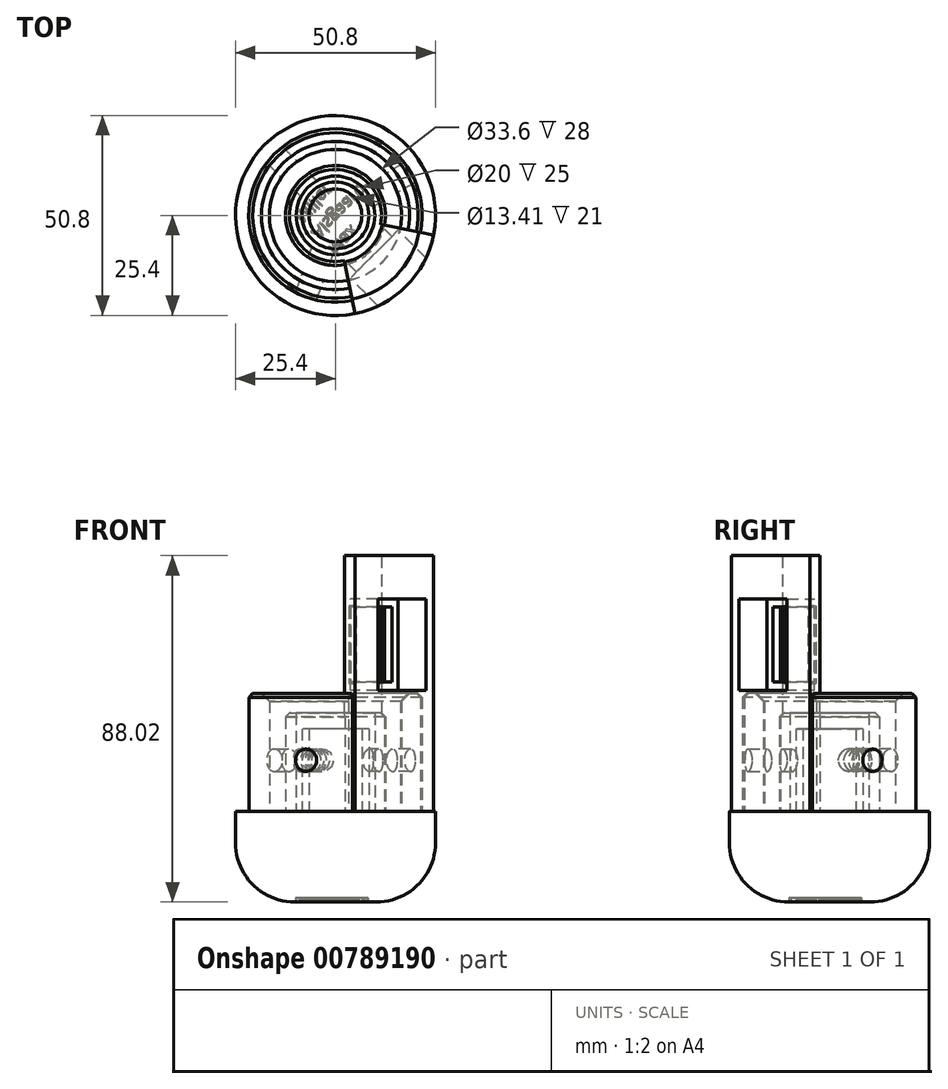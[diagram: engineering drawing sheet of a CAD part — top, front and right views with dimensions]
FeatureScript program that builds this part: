
annotation { "Feature Type Name" : "Feature", "Feature Type Description" : "" }
export const myFeature = defineFeature(function(context is Context, id is Id, definition is map)
    precondition{}
    {
        {
            var Q0;
            Q0=qCreatedBy(makeId("Right.planeOp"),FACE);
            var sketch = newSketch(context, id + "F0", { "sketchPlane" : qUnion([Q0])});
            skLineSegment(sketch, "E0", {"start": v(0, 22.52) * mm, "end": v(0, -20.14) * mm, "construction": true});
            skSolve(sketch);
        }
        {
            var Q0;
            Q0=qCreatedBy(makeId("Top.planeOp"),FACE);
            var sketch = newSketch(context, id + "F1", { "sketchPlane" : qUnion([Q0])});
            skCircle(sketch, "E1", {"center": v(0, 0) * mm, "radius": 25.4 * mm});
            skCircle(sketch, "E2", {"center": v(0, 0) * mm, "radius": 22.03 * mm});
            skCircle(sketch, "E3", {"center": v(0, 0) * mm, "radius": 16.8 * mm});
            skCircle(sketch, "E4", {"center": v(0, 0) * mm, "radius": 12.69 * mm});
            skCircle(sketch, "E5", {"center": v(0, 0) * mm, "radius": 10 * mm});
            skSolve(sketch);
        }
        {
            var Q0;
            Q0=qCreatedBy(makeId("Right.planeOp"),FACE);
            var Q1;
            Q1=sQuery(id+"F0.wireOp",EDGE,"E0");
            cPlane(context, id + "F2", {"entities" : qUnion([Q0, Q1]), "cplaneType" : CPlaneType.LINE_ANGLE, "offset" : 25 * mm, "angle" : 30 * degree, "oppositeDirection" : true, "width" : 150 * mm, "height" : 150 * mm});
        }
        {
            var Q0;
            Q0=qCreatedBy(makeId("Front.planeOp"),FACE);
            var Q1;
            Q1=sQuery(id+"F0.wireOp",EDGE,"E0");
            cPlane(context, id + "F3", {"entities" : qUnion([Q0, Q1]), "cplaneType" : CPlaneType.LINE_ANGLE, "offset" : 25 * mm, "angle" : 20 * degree, "width" : 150 * mm, "height" : 150 * mm});
        }
        {
            var Q0;
            Q0=makeQuery(id+"F1.imprint","IMPRINT",FACE,{"disambiguationData":[TD([[makeQuery(id+"F1.imprint","IMPRINT",EDGE,{"derivedFrom":sQuery(id+"F1.wireOp",EDGE,"E1")}),1.0]])]});
            var Q1;
            Q1=makeQuery(id+"F1.imprint","IMPRINT",FACE,{"disambiguationData":[TD([[makeQuery(id+"F1.imprint","IMPRINT",EDGE,{"derivedFrom":sQuery(id+"F1.wireOp",EDGE,"E2")}),1.0]])]});
            var Q2;
            Q2=makeQuery(id+"F1.imprint","IMPRINT",FACE,{"disambiguationData":[TD([[makeQuery(id+"F1.imprint","IMPRINT",EDGE,{"derivedFrom":sQuery(id+"F1.wireOp",EDGE,"E3")}),1.0]])]});
            var Q3;
            Q3=makeQuery(id+"F1.imprint","IMPRINT",FACE,{"disambiguationData":[TD([[makeQuery(id+"F1.imprint","IMPRINT",EDGE,{"derivedFrom":sQuery(id+"F1.wireOp",EDGE,"E4")}),1.0]])]});
            var Q4;
            Q4=makeQuery(id+"F1.imprint","IMPRINT",FACE,{"disambiguationData":[TD([[makeQuery(id+"F1.imprint","IMPRINT",EDGE,{"derivedFrom":sQuery(id+"F1.wireOp",EDGE,"E5")}),1.0]])]});
            extrude(context, id + "F4", {"entities" : qUnion([Q0, Q1, Q2, Q3, Q4]), "oppositeDirection" : true, "depth" : 8 * mm, "offsetDistance" : 25 * mm});
        }
        {
            var Q0;
            Q0=makeQuery(id+"F1.imprint","IMPRINT",FACE,{"disambiguationData":[TD([[makeQuery(id+"F1.imprint","IMPRINT",EDGE,{"derivedFrom":sQuery(id+"F1.wireOp",EDGE,"E2")}),1.0]])]});
            extrude(context, id + "F5", {"entities" : qUnion([Q0]), "operationType" : NewBodyOperationType.ADD, "depth" : 30 * mm, "offsetDistance" : 25 * mm});
        }
        {
            var Q0;
            Q0=makeQuery(id+"F1.imprint","IMPRINT",FACE,{"disambiguationData":[TD([[makeQuery(id+"F1.imprint","IMPRINT",EDGE,{"derivedFrom":sQuery(id+"F1.wireOp",EDGE,"E4")}),1.0]])]});
            extrude(context, id + "F6", {"entities" : qUnion([Q0]), "operationType" : NewBodyOperationType.ADD, "depth" : 25 * mm, "offsetDistance" : 25 * mm});
        }
        {
            var Q0;
            Q0=qCreatedBy(id+"F2.planeOp",FACE);
            var sketch = newSketch(context, id + "F7", { "sketchPlane" : qUnion([Q0])});
            skCircle(sketch, "E6", {"center": v(0, 13) * mm, "radius": 2.85 * mm});
            skSolve(sketch);
        }
        {
            var Q0;
            Q0=qCreatedBy(id+"F3.planeOp",FACE);
            var sketch = newSketch(context, id + "F8", { "sketchPlane" : qUnion([Q0])});
            skCircle(sketch, "E7", {"center": v(0, 13) * mm, "radius": 2.85 * mm});
            skLineSegment(sketch, "E8", {"start": v(0, -1.69) * mm, "end": v(0, 3.4) * mm, "construction": true});
            skSolve(sketch);
        }
        {
            var Q0;
            Q0=qSketchRegion(id+"F8",true);
            extrude(context, id + "F9", {"entities" : qUnion([Q0]), "operationType" : NewBodyOperationType.REMOVE, "oppositeDirection" : true, "depth" : 25 * mm, "offsetDistance" : 25 * mm, "hasSecondDirection" : true, "secondDirectionOppositeDirection" : false, "secondDirectionDepth" : 0 * mm});
        }
        {
            var Q0;
            Q0=qSketchRegion(id+"F7",true);
            var Q1;
            Q1=sQuery(id+"F7.wireOp",EDGE,"E6");
            extrude(context, id + "F10", {"entities" : qUnion([Q0]), "operationType" : NewBodyOperationType.REMOVE, "surfaceEntities" : qUnion([Q1]), "depth" : 0 * mm, "offsetDistance" : 25 * mm, "hasSecondDirection" : true, "secondDirectionOppositeDirection" : true, "secondDirectionDepth" : 25 * mm});
        }
        {
            var Q0;
            Q0=qCreatedBy(makeId("Front.planeOp"),FACE);
            var Q1;
            Q1=qCreatedBy(makeId("Right.planeOp"),FACE);
            cPlane(context, id + "F11", {"entities" : qUnion([Q0, Q1]), "cplaneType" : CPlaneType.MID_PLANE, "offset" : 25 * mm, "width" : 150 * mm, "height" : 150 * mm});
        }
        {
            var Q0;
            Q0=qCreatedBy(id+"F11.planeOp",FACE);
            var sketch = newSketch(context, id + "F12", { "sketchPlane" : qUnion([Q0])});
            skLineSegment(sketch, "E9", {"start": v(21.68, 65) * mm, "end": v(21.68, 0) * mm});
            skLineSegment(sketch, "E10", {"start": v(21.68, 0) * mm, "end": v(25.41, 0) * mm});
            skLineSegment(sketch, "E11", {"start": v(25.41, 0) * mm, "end": v(25.41, 65) * mm});
            skLineSegment(sketch, "E12", {"start": v(25.41, 65) * mm, "end": v(21.68, 65) * mm});
            skLineSegment(sketch, "E13.bottom", {"start": v(21.68, 0.02) * mm, "end": v(12.08, 0.02) * mm});
            skLineSegment(sketch, "E13.top", {"start": v(21.68, 65.02) * mm, "end": v(12.08, 65.02) * mm});
            skLineSegment(sketch, "E13.left", {"start": v(21.68, 0.02) * mm, "end": v(21.68, 65.02) * mm});
            skLineSegment(sketch, "E13.right", {"start": v(12.08, 0.02) * mm, "end": v(12.08, 65.02) * mm});
            skSolve(sketch);
        }
        {
            var Q0;
            {var subQ1=sQuery(id+"F12.wireOp",EDGE,"E9");Q0=makeQuery(id+"F12.imprint","IMPRINT",FACE,{"disambiguationData":[TD([[makeQuery(id+"F12.imprint","IMPRINT",EDGE,{"derivedFrom":subQ1}),1.0]])]});}
            var Q1;
            {var subQ3=sQuery(id+"F12.wireOp",EDGE,"E13.bottom");Q1=makeQuery(id+"F12.imprint","IMPRINT",FACE,{"disambiguationData":[TD([[makeQuery(id+"F12.imprint","IMPRINT",EDGE,{"derivedFrom":subQ3}),-1.0]])]});}
            var Q2;
            Q2=sQuery(id+"F8.wireOp",EDGE,"E8");
            revolve(context, id + "F13", {"operationType" : NewBodyOperationType.ADD, "surfaceOperationType" : NewSurfaceOperationType.NEW, "entities" : qUnion([Q0, Q1]), "axis" : qUnion([Q2]), "revolveType" : RevolveType.SYMMETRIC, "angle" : 67.67 * degree});
        }
        {
            var Q0;
            Q0=qCreatedBy(id+"F11.planeOp",FACE);
            var sketch = newSketch(context, id + "F14", { "sketchPlane" : qUnion([Q0])});
            skLineSegment(sketch, "E14.bottom", {"start": v(25.41, 30.8) * mm, "end": v(13.91, 30.8) * mm});
            skLineSegment(sketch, "E14.top", {"start": v(25.41, 54) * mm, "end": v(13.91, 54) * mm});
            skLineSegment(sketch, "E14.left", {"start": v(25.41, 30.8) * mm, "end": v(25.41, 54) * mm});
            skLineSegment(sketch, "E14.right", {"start": v(13.91, 30.8) * mm, "end": v(13.91, 54) * mm});
            skLineSegment(sketch, "E15", {"start": v(25.41, 65) * mm, "end": v(25.41, 0) * mm});
            skLineSegment(sketch, "E16", {"start": v(25.41, 65) * mm, "end": v(25.41, 0) * mm, "construction": true});
            skSolve(sketch);
        }
        {
            var Q0;
            Q0=qSketchRegion(id+"F14",true);
            extrude(context, id + "F15", {"entities" : qUnion([Q0]), "operationType" : NewBodyOperationType.REMOVE, "oppositeDirection" : true, "depth" : 8.6 * mm, "offsetDistance" : 25 * mm, "hasSecondDirection" : true, "secondDirectionOppositeDirection" : false, "secondDirectionDepth" : 8.6 * mm});
        }
        {
            var Q0;
            Q0=qCreatedBy(makeId("Right.planeOp"),FACE);
            var Q1;
            Q1=qCreatedBy(makeId("Front.planeOp"),FACE);
            cPlane(context, id + "F16", {"entities" : qUnion([Q0, Q1]), "cplaneType" : CPlaneType.MID_PLANE, "offset" : 25 * mm, "flipAlignment" : true, "width" : 150 * mm, "height" : 150 * mm});
        }
        {
            var Q0;
            Q0=qCreatedBy(id+"F16.planeOp",FACE);
            cPlane(context, id + "F17", {"entities" : qUnion([Q0]), "cplaneType" : CPlaneType.OFFSET, "offset" : 25.4 * mm, "width" : 150 * mm, "height" : 150 * mm});
        }
        {
            var Q0;
            Q0=qCreatedBy(id+"F11.planeOp",FACE);
            var sketch = newSketch(context, id + "F18", { "sketchPlane" : qUnion([Q0])});
            skLineSegment(sketch, "E17.0", {"start": v(13.91, 30.8) * mm, "end": v(13.91, 54) * mm});
            skLineSegment(sketch, "E18.0", {"start": v(25.41, 54) * mm, "end": v(13.91, 54) * mm});
            skLineSegment(sketch, "E19.0", {"start": v(25.41, 30.8) * mm, "end": v(13.91, 30.8) * mm});
            skLineSegment(sketch, "E20.bottom", {"start": v(13.91, 51.9) * mm, "end": v(11.22, 51.9) * mm});
            skLineSegment(sketch, "E20.top", {"start": v(13.91, 32.9) * mm, "end": v(11.22, 32.9) * mm});
            skLineSegment(sketch, "E20.left", {"start": v(13.91, 51.9) * mm, "end": v(13.91, 32.9) * mm});
            skLineSegment(sketch, "E20.right", {"start": v(11.22, 51.9) * mm, "end": v(11.22, 32.9) * mm});
            skSolve(sketch);
        }
        {
            var Q0;
            Q0=makeQuery(id+"F18.imprint","IMPRINT",FACE,{"disambiguationData":[TD([[makeQuery(id+"F18.imprint","IMPRINT",EDGE,{"derivedFrom":sQuery(id+"F18.wireOp",EDGE,"E20.bottom")}),1.0]])]});
            extrude(context, id + "F19", {"entities" : qUnion([Q0]), "operationType" : NewBodyOperationType.REMOVE, "endBound" : BoundingType.SYMMETRIC, "oppositeDirection" : true, "depth" : 12.68 * mm, "offsetDistance" : 25 * mm});
        }
        {
            var Q0;
            Q0=qCreatedBy(id+"F11.planeOp",FACE);
            var sketch = newSketch(context, id + "F20", { "sketchPlane" : qUnion([Q0])});
            skLineSegment(sketch, "E21.0.0", {"start": v(25.41, 30.8) * mm, "end": v(25.41, 54) * mm});
            skLineSegment(sketch, "E21.0.1", {"start": v(25.41, 54) * mm, "end": v(13.91, 54) * mm});
            skLineSegment(sketch, "E21.0.2", {"start": v(13.91, 54) * mm, "end": v(13.91, 30.8) * mm});
            skLineSegment(sketch, "E21.0.3", {"start": v(13.91, 30.8) * mm, "end": v(25.41, 30.8) * mm});
            skLineSegment(sketch, "E22.0.0", {"start": v(13.91, 32.9) * mm, "end": v(13.91, 51.9) * mm});
            skLineSegment(sketch, "E22.0.1", {"start": v(13.91, 51.9) * mm, "end": v(11.22, 51.9) * mm});
            skLineSegment(sketch, "E22.0.2", {"start": v(11.22, 51.9) * mm, "end": v(11.22, 32.9) * mm});
            skLineSegment(sketch, "E22.0.3", {"start": v(11.22, 32.9) * mm, "end": v(13.91, 32.9) * mm});
            skLineSegment(sketch, "E23", {"start": v(11.22, 42.4) * mm, "end": v(3.36, 42.4) * mm, "construction": true});
            skLineSegment(sketch, "E24.bottom", {"start": v(11.22, 52.25) * mm, "end": v(8.97, 52.25) * mm});
            skLineSegment(sketch, "E24.top", {"start": v(11.22, 32.55) * mm, "end": v(8.97, 32.55) * mm});
            skLineSegment(sketch, "E24.left", {"start": v(11.22, 52.25) * mm, "end": v(11.22, 32.55) * mm});
            skLineSegment(sketch, "E24.right", {"start": v(8.97, 52.25) * mm, "end": v(8.97, 32.55) * mm});
            skPoint(sketch, "E24.middle", {"position": v(10.1, 42.4) * mm});
            skSolve(sketch);
        }
        {
            var Q0;
            {var subQ3=sQuery(id+"F20.wireOp",EDGE,"E24.bottom");Q0=makeQuery(id+"F20.imprint","IMPRINT",FACE,{"disambiguationData":[TD([[makeQuery(id+"F20.imprint","IMPRINT",EDGE,{"derivedFrom":subQ3}),1.0]])]});}
            extrude(context, id + "F21", {"entities" : qUnion([Q0]), "operationType" : NewBodyOperationType.REMOVE, "endBound" : BoundingType.SYMMETRIC, "oppositeDirection" : true, "depth" : 11.6 * mm, "offsetDistance" : 25 * mm});
        }
        {
            var Q0;
            Q0=makeQuery(id+"F4.opExtrude","CAP_FACE",FACE,{"disambiguationData":[OSD([sQuery(id+"F1.wireOp",EDGE,"E1")])],"isStart":false});
            cPlane(context, id + "F22", {"entities" : qUnion([Q0]), "cplaneType" : CPlaneType.OFFSET, "offset" : 0 * mm, "width" : 150 * mm, "height" : 150 * mm});
        }
        {
            var Q0;
            Q0=qCreatedBy(id+"F22.planeOp",FACE);
            var sketch = newSketch(context, id + "F23", { "sketchPlane" : qUnion([Q0])});
            skCircle(sketch, "E25.0.0", {"center": v(0, 0) * mm, "radius": 25.4 * mm});
            skSolve(sketch);
        }
        {
            var Q0;
            Q0=makeQuery(id+"F23.imprint","IMPRINT",FACE,{"disambiguationData":[TD([[makeQuery(id+"F23.imprint","IMPRINT",EDGE,{"derivedFrom":sQuery(id+"F23.wireOp",EDGE,"E25.0.0")}),1.0]])]});
            extrude(context, id + "F24", {"entities" : qUnion([Q0]), "operationType" : NewBodyOperationType.ADD, "surfaceOperationType" : NewSurfaceOperationType.ADD, "depth" : 15 * mm, "offsetDistance" : 25 * mm});
        }
        {
            var Q0;
            Q0=makeQuery(id+"F24.opExtrude","CAP_EDGE",EDGE,{"disambiguationData":[OSD([sQuery(id+"F23.wireOp",EDGE,"E25.0.0")])],"isStart":false});
            fillet(context, id + "F25", {"entities" : qUnion([Q0]), "radius" : 15 * mm, "tangentPropagation" : true, "allowEdgeOverflow" : false});
        }
        {
            var Q0;
            Q0=qCreatedBy(id+"F22.planeOp",FACE);
            cPlane(context, id + "F26", {"entities" : qUnion([Q0]), "cplaneType" : CPlaneType.OFFSET, "offset" : 15 * mm, "width" : 150 * mm, "height" : 150 * mm});
        }
        {
            var Q0;
            Q0=qCreatedBy(id+"F26.planeOp",FACE);
            var sketch = newSketch(context, id + "F27", { "sketchPlane" : qUnion([Q0])});
            skText(sketch, "E26", { "text": "Max\nAlsgaard\nMiller", "fontName": "OpenSans-Regular.ttf"});
            const initialGuessF27  = {"E26": [-0.0021, 0.00836, 0.7071, -0.7071, 0.00315]};
            skSetInitialGuess(sketch, initialGuessF27);
            skSolve(sketch);
        }
        {
            var Q0;
            Q0 = qSketchRegion(id + "F27", true);
            extrude(context, id + "F28", {"entities" : qUnion([Q0]), "operationType" : NewBodyOperationType.REMOVE, "oppositeDirection" : true, "depth" : 1 * mm, "offsetDistance" : 25 * mm});
        }
        {
            var Q0;
            Q0=qCreatedBy(makeId("Top.planeOp"),FACE);
            var sketch = newSketch(context, id + "F29", { "sketchPlane" : qUnion([Q0])});
            skCircle(sketch, "E27", {"center": v(0, 0) * mm, "radius": 6.7 * mm});
            skCircle(sketch, "E28", {"center": v(0, 0) * mm, "radius": 8.5 * mm});
            skSolve(sketch);
        }
        {
            var Q0;
            Q0=makeQuery(id+"F29.imprint","IMPRINT",FACE,{"disambiguationData":[TD([[makeQuery(id+"F29.imprint","IMPRINT",EDGE,{"derivedFrom":sQuery(id+"F29.wireOp",EDGE,"E27")}),-1.0]])]});
            extrude(context, id + "F30", {"entities" : qUnion([Q0]), "operationType" : NewBodyOperationType.ADD, "depth" : 21 * mm, "offsetDistance" : 25 * mm});
        }
        {
            var Q0;
            Q0=qCreatedBy(id+"F16.planeOp",FACE);
            var sketch = newSketch(context, id + "F31", { "sketchPlane" : qUnion([Q0])});
            skLineSegment(sketch, "E29.0", {"start": v(-25.4, 0) * mm, "end": v(25.4, 0) * mm});
            skCircle(sketch, "E30", {"center": v(0, 13) * mm, "radius": 2.85 * mm});
            skSolve(sketch);
        }
        {
            var Q0;
            Q0 = qSketchRegion(id + "F31", true);
            extrude(context, id + "F32", {"entities" : qUnion([Q0]), "operationType" : NewBodyOperationType.REMOVE, "oppositeDirection" : true, "depth" : 25 * mm, "offsetDistance" : 25 * mm});
        }
        {
            var Q0;
            Q0=makeQuery(id+"F5.opExtrude","CAP_EDGE",EDGE,{"disambiguationData":[OSD([sQuery(id+"F1.wireOp",EDGE,"E3")])],"isStart":false});
            chamfer(context, id + "F33", {"entities" : qUnion([Q0]), "width" : 2 * mm, "tangentPropagation" : true});
        }
        {
            var Q0;
            Q0=makeQuery(id+"F6.opExtrude","CAP_EDGE",EDGE,{"disambiguationData":[OSD([sQuery(id+"F1.wireOp",EDGE,"E4")])],"isStart":false});
            chamfer(context, id + "F34", {"entities" : qUnion([Q0]), "width" : 1 * mm, "tangentPropagation" : true});
        }
        {
            var Q0;
            Q0=makeQuery(id+"F5.opExtrude","CAP_EDGE",EDGE,{"disambiguationData":[OSD([sQuery(id+"F1.wireOp",EDGE,"E2")])],"isStart":false});
            chamfer(context, id + "F35", {"entities" : qUnion([Q0]), "width" : 1 * mm, "tangentPropagation" : true});
        }
    });
